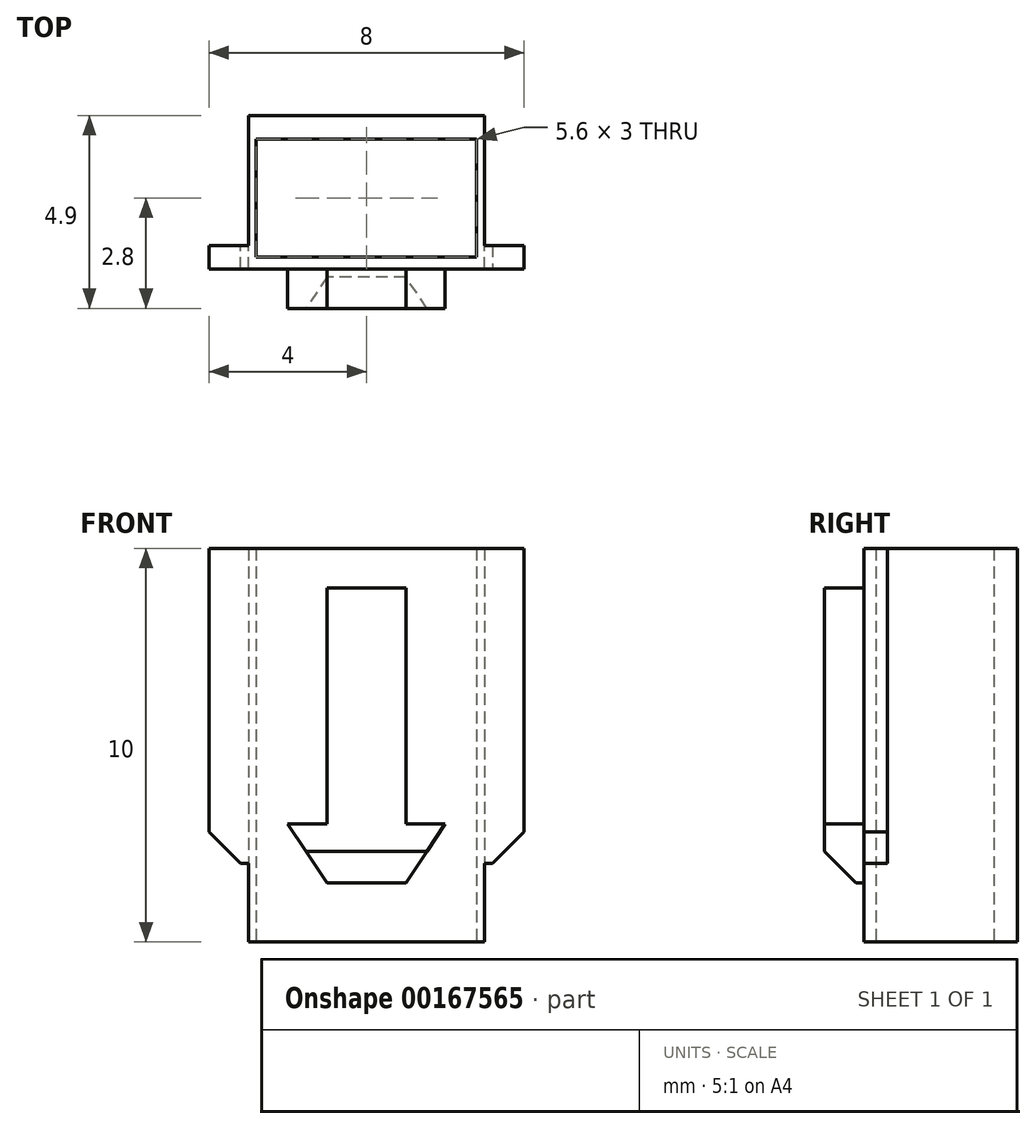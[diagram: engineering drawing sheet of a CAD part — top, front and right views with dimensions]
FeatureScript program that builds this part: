
annotation { "Feature Type Name" : "Feature", "Feature Type Description" : "" }
export const myFeature = defineFeature(function(context is Context, id is Id, definition is map)
    precondition{}
    {
        {
            var Q0;
            Q0=qCreatedBy(makeId("Top.planeOp"),FACE);
            var sketch = newSketch(context, id + "F0", { "sketchPlane" : qUnion([Q0])});
            skLineSegment(sketch, "E0.bottom", {"start": v(-3, 1.95) * mm, "end": v(3, 1.95) * mm});
            skLineSegment(sketch, "E0.top", {"start": v(-3, -1.95) * mm, "end": v(3, -1.95) * mm});
            skLineSegment(sketch, "E0.left", {"start": v(-3, 1.95) * mm, "end": v(-3, -1.95) * mm});
            skLineSegment(sketch, "E0.right", {"start": v(3, 1.95) * mm, "end": v(3, -1.95) * mm});
            skPoint(sketch, "E0.middle", {"position": v(0, 0) * mm});
            skLineSegment(sketch, "E1.bottom", {"start": v(-2.8, 1.35) * mm, "end": v(2.8, 1.35) * mm});
            skLineSegment(sketch, "E1.top", {"start": v(-2.8, -1.65) * mm, "end": v(2.8, -1.65) * mm});
            skLineSegment(sketch, "E1.left", {"start": v(-2.8, 1.35) * mm, "end": v(-2.8, -1.65) * mm});
            skLineSegment(sketch, "E1.right", {"start": v(2.8, 1.35) * mm, "end": v(2.8, -1.65) * mm});
            skPoint(sketch, "E1.middle", {"position": v(0, -0.15) * mm});
            skSolve(sketch);
        }
        {
            var Q0;
            Q0=makeQuery(id+"F0.imprint","IMPRINT",FACE,{"disambiguationData":[TD([[makeQuery(id+"F0.imprint","IMPRINT",EDGE,{"derivedFrom":sQuery(id+"F0.wireOp",EDGE,"E0.bottom")}),-1.0]])]});
            extrude(context, id + "F1", {"entities" : qUnion([Q0]), "depth" : 10 * mm});
        }
        {
            var Q0;
            Q0=makeQuery(id+"F1.opExtrude","SWEPT_FACE",FACE,{"disambiguationData":[OSD([sQuery(id+"F0.wireOp",EDGE,"E0.top")])]});
            var sketch = newSketch(context, id + "F2", { "sketchPlane" : qUnion([Q0])});
            skLineSegment(sketch, "E2", {"start": v(-1, 9) * mm, "end": v(-1, 3) * mm});
            skLineSegment(sketch, "E3", {"start": v(-1, 3) * mm, "end": v(-2, 3) * mm});
            skLineSegment(sketch, "E4", {"start": v(-2, 3) * mm, "end": v(-1, 1.5) * mm});
            skLineSegment(sketch, "E5", {"start": v(-1, 1.5) * mm, "end": v(0, 1.5) * mm});
            skLineSegment(sketch, "E6", {"start": v(0, 1.5) * mm, "end": v(0, 8) * mm});
            skLineSegment(sketch, "E7.MirrorCS", {"start": v(1, 1.5) * mm, "end": v(0, 1.5) * mm});
            skLineSegment(sketch, "E8.MirrorCS", {"start": v(2, 3) * mm, "end": v(1, 1.5) * mm});
            skLineSegment(sketch, "E9.MirrorCS", {"start": v(1, 3) * mm, "end": v(2, 3) * mm});
            skLineSegment(sketch, "E10.MirrorCS", {"start": v(1, 9) * mm, "end": v(1, 3) * mm});
            skLineSegment(sketch, "E11", {"start": v(0, 8) * mm, "end": v(0, 8) * mm});
            skLineSegment(sketch, "E12", {"start": v(-1, 9) * mm, "end": v(1, 9) * mm});
            skSolve(sketch);
        }
        {
            var Q0;
            {var subQ0=sQuery(id+"F2.wireOp",EDGE,"E2");Q0=makeQuery(id+"F2.imprint","IMPRINT",FACE,{"disambiguationData":[TD([[makeQuery(id+"F2.imprint","IMPRINT",EDGE,{"derivedFrom":subQ0}),1.0]])]});}
            var Q1;
            {var subQ0=sQuery(id+"F2.wireOp",EDGE,"E6");Q1=makeQuery(id+"F2.imprint","IMPRINT",FACE,{"disambiguationData":[TD([[makeQuery(id+"F2.imprint","IMPRINT",EDGE,{"derivedFrom":subQ0}),-1.0]])]});}
            extrude(context, id + "F3", {"entities" : qUnion([Q0, Q1]), "operationType" : NewBodyOperationType.ADD, "depth" : 1 * mm});
        }
        {
            var Q0;
            Q0=makeQuery(id+"F3.opExtrude","CAP_EDGE",EDGE,{"disambiguationData":[OSD([sQuery(id+"F2.wireOp",EDGE,"E7.MirrorCS")])],"isStart":false});
            var Q1;
            Q1=makeQuery(id+"F3.opExtrude","CAP_EDGE",EDGE,{"disambiguationData":[OSD([sQuery(id+"F2.wireOp",EDGE,"E5")])],"isStart":false});
            chamfer(context, id + "F4", {"entities" : qUnion([Q0, Q1]), "width" : 0.8 * mm, "tangentPropagation" : true});
        }
        {
            var Q0;
            Q0=makeQuery(id+"F1.opExtrude","SWEPT_FACE",FACE,{"disambiguationData":[OSD([sQuery(id+"F0.wireOp",EDGE,"E0.right")])]});
            var sketch = newSketch(context, id + "F5", { "sketchPlane" : qUnion([Q0])});
            skLineSegment(sketch, "E13.bottom", {"start": v(-1.95, 10) * mm, "end": v(-1.35, 10) * mm});
            skLineSegment(sketch, "E13.top", {"start": v(-1.95, 2) * mm, "end": v(-1.35, 2) * mm});
            skLineSegment(sketch, "E13.left", {"start": v(-1.95, 10) * mm, "end": v(-1.95, 2) * mm});
            skLineSegment(sketch, "E13.right", {"start": v(-1.35, 10) * mm, "end": v(-1.35, 2) * mm});
            skSolve(sketch);
        }
        {
            var Q0;
            Q0=makeQuery(id+"F5.imprint","IMPRINT",FACE,{"disambiguationData":[TD([[makeQuery(id+"F5.imprint","IMPRINT",EDGE,{"derivedFrom":sQuery(id+"F5.wireOp",EDGE,"E13.bottom")}),1.0]])]});
            extrude(context, id + "F6", {"entities" : qUnion([Q0]), "operationType" : NewBodyOperationType.ADD, "depth" : 1 * mm});
        }
        {
            var Q0;
            Q0=makeQuery(id+"F6.opExtrude","CAP_EDGE",EDGE,{"disambiguationData":[OSD([sQuery(id+"F5.wireOp",EDGE,"E13.top")])],"isStart":false});
            chamfer(context, id + "F7", {"entities" : qUnion([Q0]), "width" : 0.8 * mm, "tangentPropagation" : true});
        }
        {
            var Q0;
            Q0=makeQuery(id+"F1.opExtrude","SWEPT_FACE",FACE,{"disambiguationData":[OSD([sQuery(id+"F0.wireOp",EDGE,"E0.left")])]});
            var sketch = newSketch(context, id + "F8", { "sketchPlane" : qUnion([Q0])});
            skPoint(sketch, "E14.oppositeSnap0", {"position": v(1.35, 13.88) * mm});
            skLineSegment(sketch, "E14.bottom", {"start": v(1.95, 10) * mm, "end": v(1.35, 10) * mm});
            skLineSegment(sketch, "E14.top", {"start": v(1.95, 2) * mm, "end": v(1.35, 2) * mm});
            skLineSegment(sketch, "E14.left", {"start": v(1.95, 10) * mm, "end": v(1.95, 2) * mm});
            skLineSegment(sketch, "E14.right", {"start": v(1.35, 10) * mm, "end": v(1.35, 2) * mm});
            skSolve(sketch);
        }
        {
            var Q0;
            Q0=makeQuery(id+"F8.imprint","IMPRINT",FACE,{"disambiguationData":[TD([[makeQuery(id+"F8.imprint","IMPRINT",EDGE,{"derivedFrom":sQuery(id+"F8.wireOp",EDGE,"E14.bottom")}),-1.0]])]});
            extrude(context, id + "F9", {"entities" : qUnion([Q0]), "operationType" : NewBodyOperationType.ADD, "depth" : 1 * mm});
        }
        {
            var Q0;
            Q0=makeQuery(id+"F9.opExtrude","CAP_EDGE",EDGE,{"disambiguationData":[OSD([sQuery(id+"F8.wireOp",EDGE,"E14.top")])],"isStart":false});
            chamfer(context, id + "F10", {"entities" : qUnion([Q0]), "width" : 0.8 * mm, "tangentPropagation" : true});
        }
    });
